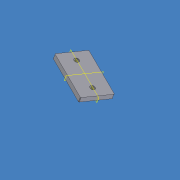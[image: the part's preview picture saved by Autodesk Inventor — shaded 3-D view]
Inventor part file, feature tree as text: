
AUTODESK INVENTOR PART (.ipt)
format: ipt  version: 2015 (Build 190159000, 159)  size: 105,984 bytes
history: native  units: mm
features: plane x2, sheet_metal_op x1, hole x1, mirror x1, chamfer x1, sketch x1, other x1
ambient origin geometry x8: Origin, YZ Plane, XZ Plane, XY Plane, X Axis, Y Axis, Z Axis, Center Point
bodies: Solid1 (feature_tree)
feature tree (8):
  sheet_metal_op  "Face1"
  hole  "Hole1"  [1 undecoded]
  plane  "Work Plane1"
  plane  "Work Plane2"
  mirror  "Mirror1"
  chamfer  "Corner Round1"
  sketch  "Sketch1"  dims[d2=80.0mm d3=50.0mm d4=0.001mm d5=15.0mm d6=25.0mm d7=8.376mm d8=6.0mm d9=4.0mm d10=2.0mm d11=90.0deg d12=8.0mm d13=20.594885mm d14=1.0mm]
  other  "Plate1"
note: 1 required parameter value undecoded (feature->parameter linkage not recoverable at this tier; creation-order binding heuristic only, values carry confidence <= 0.55)
